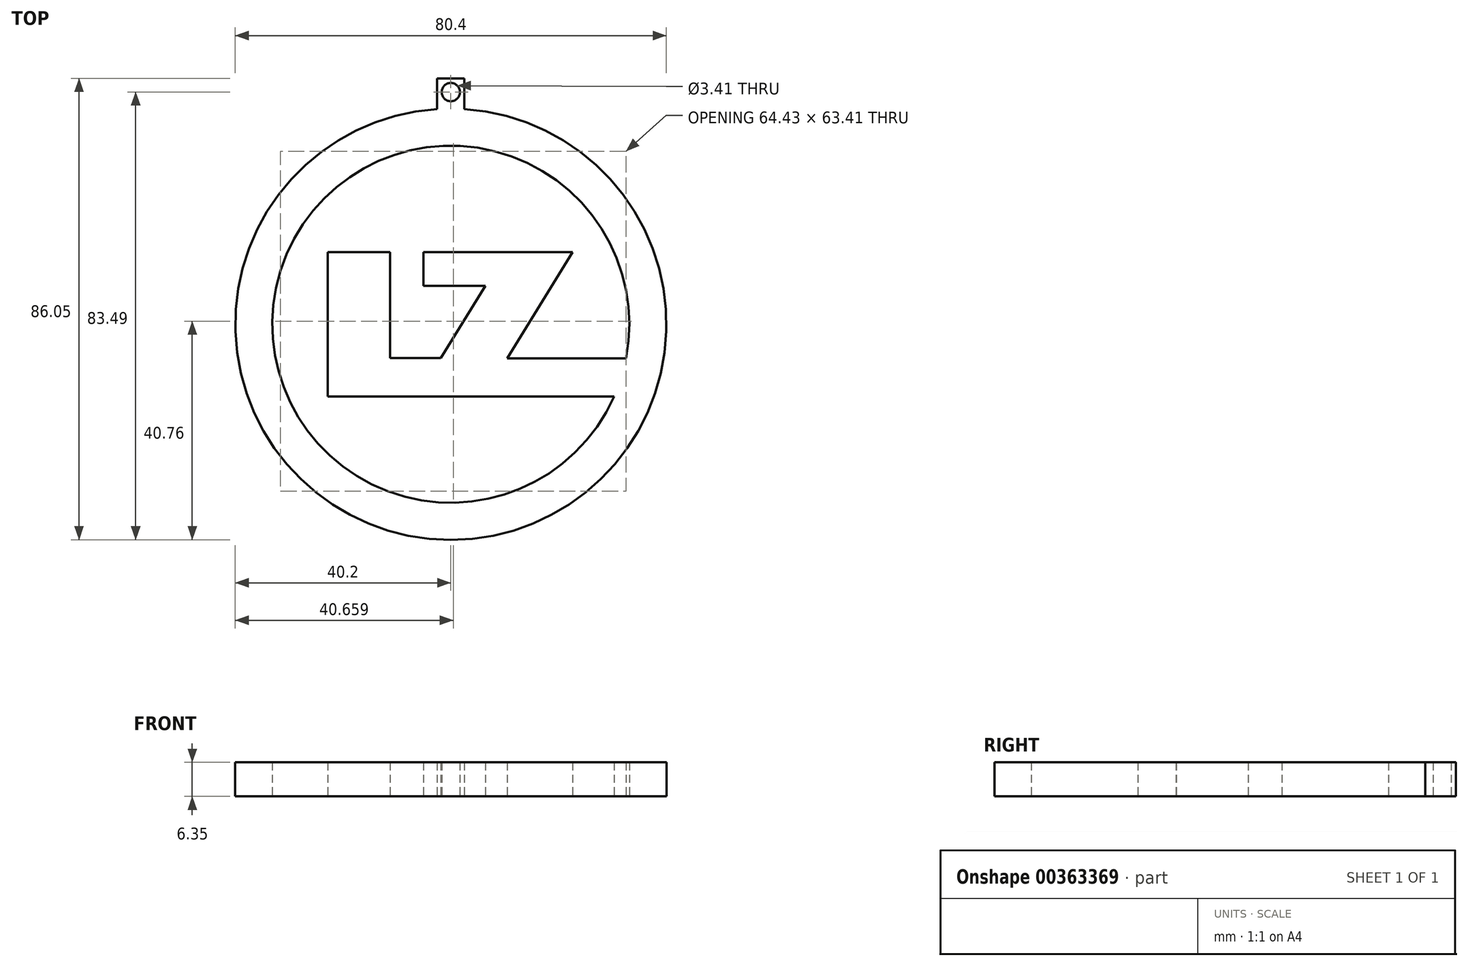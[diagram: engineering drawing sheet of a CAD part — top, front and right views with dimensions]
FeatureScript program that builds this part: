
annotation { "Feature Type Name" : "Feature", "Feature Type Description" : "" }
export const myFeature = defineFeature(function(context is Context, id is Id, definition is map)
    precondition{}
    {
        {
            var Q0;
            Q0=qCreatedBy(makeId("Top.planeOp"),FACE);
            var sketch = newSketch(context, id + "F0", { "sketchPlane" : qUnion([Q0])});
            skArc(sketch, "E0", {"start": v(-2.54, 40.12) * mm, "mid": v(0, -40.2) * mm, "end": v(2.54, 40.12) * mm});
            skArc(sketch, "E1", {"start": v(32.68, -6.35) * mm, "mid": v(-31.76, 9.98) * mm, "end": v(30.44, -13.47) * mm});
            skLineSegment(sketch, "E2", {"start": v(-22.97, 13.44) * mm, "end": v(-22.97, -13.47) * mm});
            skLineSegment(sketch, "E3", {"start": v(-22.97, -13.47) * mm, "end": v(30.44, -13.47) * mm});
            skLineSegment(sketch, "E4", {"start": v(-22.97, 13.44) * mm, "end": v(-11.32, 13.44) * mm});
            skLineSegment(sketch, "E5", {"start": v(-11.32, 13.44) * mm, "end": v(-11.32, -6.28) * mm});
            skLineSegment(sketch, "E6", {"start": v(-11.32, -6.28) * mm, "end": v(-1.85, -6.28) * mm});
            skLineSegment(sketch, "E7", {"start": v(-1.85, -6.28) * mm, "end": v(6.42, 7.15) * mm});
            skLineSegment(sketch, "E8", {"start": v(6.42, 7.15) * mm, "end": v(-5.09, 7.15) * mm});
            skLineSegment(sketch, "E9", {"start": v(-5.09, 7.15) * mm, "end": v(-5.09, 13.44) * mm});
            skLineSegment(sketch, "E10", {"start": v(-5.09, 13.44) * mm, "end": v(22.72, 13.44) * mm});
            skLineSegment(sketch, "E11", {"start": v(22.72, 13.44) * mm, "end": v(10.52, -6.35) * mm});
            skLineSegment(sketch, "E12", {"start": v(10.52, -6.35) * mm, "end": v(32.68, -6.35) * mm});
            skLineSegment(sketch, "E13", {"start": v(0, 45.85) * mm, "end": v(2.54, 45.85) * mm});
            skLineSegment(sketch, "E14", {"start": v(2.54, 45.85) * mm, "end": v(2.54, 40.12) * mm});
            skLineSegment(sketch, "E15", {"start": v(0, 45.85) * mm, "end": v(-2.54, 45.85) * mm});
            skLineSegment(sketch, "E16", {"start": v(-2.54, 45.85) * mm, "end": v(-2.54, 40.12) * mm});
            skCircle(sketch, "E17", {"center": v(0, 43.3) * mm, "radius": 1.7 * mm});
            skSolve(sketch);
        }
        {
            var Q0;
            Q0 = qSketchRegion(id + "F0", true);
            extrude(context, id + "F1", {"entities" : qUnion([Q0]), "depth" : 6.35 * mm});
        }
    });
